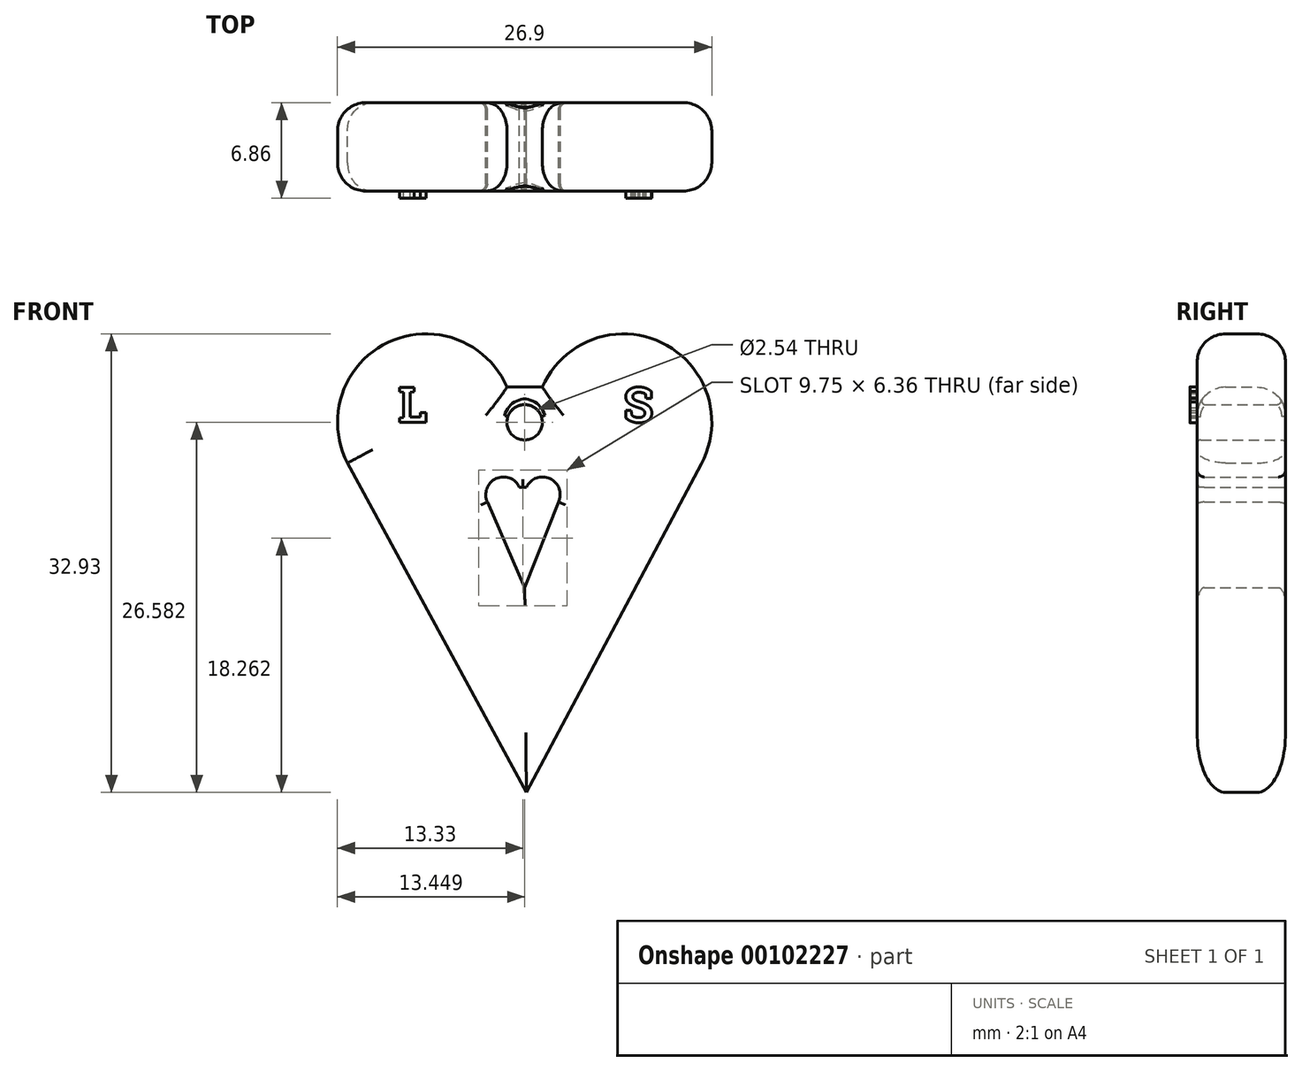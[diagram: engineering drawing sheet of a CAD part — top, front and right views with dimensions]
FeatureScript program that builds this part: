
annotation { "Feature Type Name" : "Feature", "Feature Type Description" : "" }
export const myFeature = defineFeature(function(context is Context, id is Id, definition is map)
    precondition{}
    {
        {
            var Q0;
            Q0=qCreatedBy(makeId("Front.planeOp"),FACE);
            var sketch = newSketch(context, id + "F0", { "sketchPlane" : qUnion([Q0])});
            skArc(sketch, "E0", {"start": v(-32.4, 14.4) * mm, "mid": v(-40.94, 17.6) * mm, "end": v(-43.85, 8.95) * mm});
            skArc(sketch, "E1", {"start": v(-18.42, 8.88) * mm, "mid": v(-21.27, 17.6) * mm, "end": v(-29.85, 14.4) * mm});
            skPoint(sketch, "E2.centerSnap0", {"position": v(-31.12, 11.87) * mm});
            skLineSegment(sketch, "E3", {"start": v(-31, -14.71) * mm, "end": v(-18.39, 8.95) * mm});
            skLineSegment(sketch, "E4", {"start": v(-32.4, 14.4) * mm, "end": v(-29.85, 14.4) * mm});
            skPoint(sketch, "E5.endSnap0", {"position": v(-24.65, -47.79) * mm});
            skPoint(sketch, "E2.center.orphan", {"position": v(-31.12, -35.94) * mm});
            skLineSegment(sketch, "E6", {"start": v(-43.85, 8.95) * mm, "end": v(-31, -14.71) * mm});
            skCircle(sketch, "E7", {"center": v(-31.12, 11.87) * mm, "radius": 1.27 * mm});
            skLineSegment(sketch, "E8", {"start": v(-31.12, 11.87) * mm, "end": v(-31.12, 10.6) * mm});
            skPoint(sketch, "E9.centerSnap0", {"position": v(-25.09, -1.62) * mm});
            skPoint(sketch, "E10.center.orphan", {"position": v(-20.45, -1.62) * mm});
            skPoint(sketch, "E10.start.orphan", {"position": v(-18, -3.65) * mm});
            skPoint(sketch, "E11.center.orphan", {"position": v(-29.73, -1.62) * mm});
            skPoint(sketch, "E11.end.orphan", {"position": v(-32.17, -3.65) * mm});
            skPoint(sketch, "E9.center.orphan", {"position": v(-25.09, -17.94) * mm});
            skPoint(sketch, "E9.end.orphan", {"position": v(-24.28, -18.29) * mm});
            skPoint(sketch, "E9.start.orphan", {"position": v(-25.9, -18.29) * mm});
            skPoint(sketch, "E12.orphan", {"position": v(-27, 0) * mm});
            skPoint(sketch, "E13.start.orphan", {"position": v(-42.33, -35.94) * mm});
            skPoint(sketch, "E14.center.orphan", {"position": v(-24.72, -50.93) * mm});
            skArc(sketch, "E15", {"start": v(-31.5, 7.21) * mm, "mid": v(-33.18, 7.83) * mm, "end": v(-33.8, 6.14) * mm});
            skArc(sketch, "E16", {"start": v(-28.68, 6.14) * mm, "mid": v(-29.3, 7.83) * mm, "end": v(-30.99, 7.21) * mm});
            skLineSegment(sketch, "E17", {"start": v(-30.99, 7.21) * mm, "end": v(-31.5, 7.21) * mm});
            skPoint(sketch, "E18.orphan", {"position": v(-31.12, 6.68) * mm});
            skPoint(sketch, "E19.orphan", {"position": v(-31.12, 0) * mm});
            skPoint(sketch, "E20.start.orphan", {"position": v(-33.91, 6.68) * mm});
            skLineSegment(sketch, "E21", {"start": v(-28.68, 6.14) * mm, "end": v(-31.12, 0) * mm});
            skLineSegment(sketch, "E22", {"start": v(-33.8, 6.14) * mm, "end": v(-31.12, 0) * mm});
            skPoint(sketch, "E23.start.orphan", {"position": v(-31.24, 7.21) * mm});
            skLineSegment(sketch, "E24", {"start": v(-31.12, 14.4) * mm, "end": v(-31.24, 7.21) * mm});
            skSolve(sketch);
        }
        {
            var Q0;
            Q0=makeQuery(id+"F0.imprint","IMPRINT",FACE,{"disambiguationData":[TD([[makeQuery(id+"F0.imprint","IMPRINT",EDGE,{"derivedFrom":sQuery(id+"F0.wireOp",EDGE,"E0")}),1.0]])]});
            extrude(context, id + "F1", {"entities" : qUnion([Q0]), "depth" : 6.35 * mm});
        }
        {
            var Q0;
            Q0=makeQuery(id+"F1.opExtrude","CAP_EDGE",EDGE,{"disambiguationData":[OSD([sQuery(id+"F0.wireOp",EDGE,"E0")])],"isStart":false});
            var Q1;
            Q1=makeQuery(id+"F1.opExtrude","CAP_EDGE",EDGE,{"disambiguationData":[OSD([sQuery(id+"F0.wireOp",EDGE,"E6")])],"isStart":false});
            var Q2;
            Q2=makeQuery(id+"F1.opExtrude","CAP_EDGE",EDGE,{"disambiguationData":[OSD([sQuery(id+"F0.wireOp",EDGE,"E1")])],"isStart":false});
            var Q3;
            Q3=makeQuery(id+"F1.opExtrude","CAP_EDGE",EDGE,{"disambiguationData":[OSD([sQuery(id+"F0.wireOp",EDGE,"E4")])],"isStart":false});
            var Q4;
            Q4=makeQuery(id+"F1.opExtrude","CAP_EDGE",EDGE,{"disambiguationData":[OSD([sQuery(id+"F0.wireOp",EDGE,"E0")])],"isStart":true});
            var Q5;
            Q5=makeQuery(id+"F1.opExtrude","CAP_EDGE",EDGE,{"disambiguationData":[OSD([sQuery(id+"F0.wireOp",EDGE,"E6")])],"isStart":true});
            var Q6;
            Q6=makeQuery(id+"F1.opExtrude","CAP_EDGE",EDGE,{"disambiguationData":[OSD([sQuery(id+"F0.wireOp",EDGE,"E4")])],"isStart":true});
            var Q7;
            Q7=makeQuery(id+"F1.opExtrude","CAP_EDGE",EDGE,{"disambiguationData":[OSD([sQuery(id+"F0.wireOp",EDGE,"E1")])],"isStart":true});
            fillet(context, id + "F2", {"entities" : qUnion([Q0, Q1, Q2, Q3, Q4, Q5, Q6, Q7]), "radius" : 2.03 * mm, "tangentPropagation" : true, "allowEdgeOverflow" : false});
        }
        {
            var Q0;
            Q0=makeQuery(id+"F1.opExtrude","CAP_EDGE",EDGE,{"disambiguationData":[OSD([sQuery(id+"F0.wireOp",EDGE,"E7")])],"isStart":false});
            var Q1;
            Q1=makeQuery(id+"F1.opExtrude","CAP_EDGE",EDGE,{"disambiguationData":[OSD([sQuery(id+"F0.wireOp",EDGE,"E7")])],"isStart":true});
            fillet(context, id + "F3", {"entities" : qUnion([Q0, Q1]), "radius" : 0.25 * mm, "tangentPropagation" : true, "allowEdgeOverflow" : false});
        }
        {
            var Q0;
            Q0=makeQuery(id+"F1.opExtrude","CAP_EDGE",EDGE,{"disambiguationData":[OSD([sQuery(id+"F0.wireOp",EDGE,"E16")])],"isStart":true});
            var Q1;
            Q1=makeQuery(id+"F1.opExtrude","CAP_EDGE",EDGE,{"disambiguationData":[OSD([sQuery(id+"F0.wireOp",EDGE,"E17")])],"isStart":true});
            var Q2;
            Q2=makeQuery(id+"F1.opExtrude","CAP_EDGE",EDGE,{"disambiguationData":[OSD([sQuery(id+"F0.wireOp",EDGE,"E15")])],"isStart":true});
            var Q3;
            Q3=makeQuery(id+"F1.opExtrude","CAP_EDGE",EDGE,{"disambiguationData":[OSD([sQuery(id+"F0.wireOp",EDGE,"E22")])],"isStart":true});
            var Q4;
            Q4=makeQuery(id+"F1.opExtrude","CAP_EDGE",EDGE,{"disambiguationData":[OSD([sQuery(id+"F0.wireOp",EDGE,"E21")])],"isStart":true});
            var Q5;
            Q5=makeQuery(id+"F1.opExtrude","CAP_EDGE",EDGE,{"disambiguationData":[OSD([sQuery(id+"F0.wireOp",EDGE,"E15")])],"isStart":false});
            var Q6;
            Q6=makeQuery(id+"F1.opExtrude","CAP_EDGE",EDGE,{"disambiguationData":[OSD([sQuery(id+"F0.wireOp",EDGE,"E17")])],"isStart":false});
            var Q7;
            Q7=makeQuery(id+"F1.opExtrude","CAP_EDGE",EDGE,{"disambiguationData":[OSD([sQuery(id+"F0.wireOp",EDGE,"E16")])],"isStart":false});
            var Q8;
            Q8=makeQuery(id+"F1.opExtrude","CAP_EDGE",EDGE,{"disambiguationData":[OSD([sQuery(id+"F0.wireOp",EDGE,"E21")])],"isStart":false});
            var Q9;
            Q9=makeQuery(id+"F1.opExtrude","CAP_EDGE",EDGE,{"disambiguationData":[OSD([sQuery(id+"F0.wireOp",EDGE,"E22")])],"isStart":false});
            fillet(context, id + "F4", {"entities" : qUnion([Q0, Q1, Q2, Q3, Q4, Q5, Q6, Q7, Q8, Q9]), "radius" : 0.5 * mm, "tangentPropagation" : true, "allowEdgeOverflow" : false});
        }
        {
            var Q0;
            Q0=makeQuery(id+"F1.opExtrude","CAP_FACE",FACE,{"disambiguationData":[OSD([sQuery(id+"F0.wireOp",EDGE,"E0"),sQuery(id+"F0.wireOp",EDGE,"E1"),sQuery(id+"F0.wireOp",EDGE,"E3"),sQuery(id+"F0.wireOp",EDGE,"E4"),sQuery(id+"F0.wireOp",EDGE,"E6"),sQuery(id+"F0.wireOp",EDGE,"E7"),sQuery(id+"F0.wireOp",EDGE,"E15"),sQuery(id+"F0.wireOp",EDGE,"E16"),sQuery(id+"F0.wireOp",EDGE,"E17"),sQuery(id+"F0.wireOp",EDGE,"E21"),sQuery(id+"F0.wireOp",EDGE,"E22")])],"isStart":false});
            var sketch = newSketch(context, id + "F5", { "sketchPlane" : qUnion([Q0])});
            skText(sketch, "E25", { "text": "L", "fontName": "RobotoSlab-Bold.ttf"});
            skText(sketch, "E26", { "text": "S", "fontName": "RobotoSlab-Bold.ttf"});
            const initialGuessF5  = {"E25": [-0.0402, 0.01187, 1, 0, 0.00254], "E26": [-0.02402, 0.01187, 1, 0, 0.00254]};
            skSetInitialGuess(sketch, initialGuessF5);
            skSolve(sketch);
        }
        {
            var Q0;
            Q0=makeQuery(id+"F5.imprint","IMPRINT",FACE,{"disambiguationData":[TD([[makeQuery(id+"F5.imprint","IMPRINT",EDGE,{"derivedFrom":sQuery(id+"F5.wireOp",EDGE,"E25.sketch_text.stroke-0")}),-1.0]])]});
            var Q1;
            Q1=makeQuery(id+"F5.imprint","IMPRINT",FACE,{"disambiguationData":[TD([[makeQuery(id+"F5.imprint","IMPRINT",EDGE,{"derivedFrom":sQuery(id+"F5.wireOp",EDGE,"E26.sketch_text.stroke-0")}),-1.0]])]});
            extrude(context, id + "F6", {"entities" : qUnion([Q0, Q1]), "operationType" : NewBodyOperationType.ADD, "depth" : 0.5 * mm});
        }
    });
